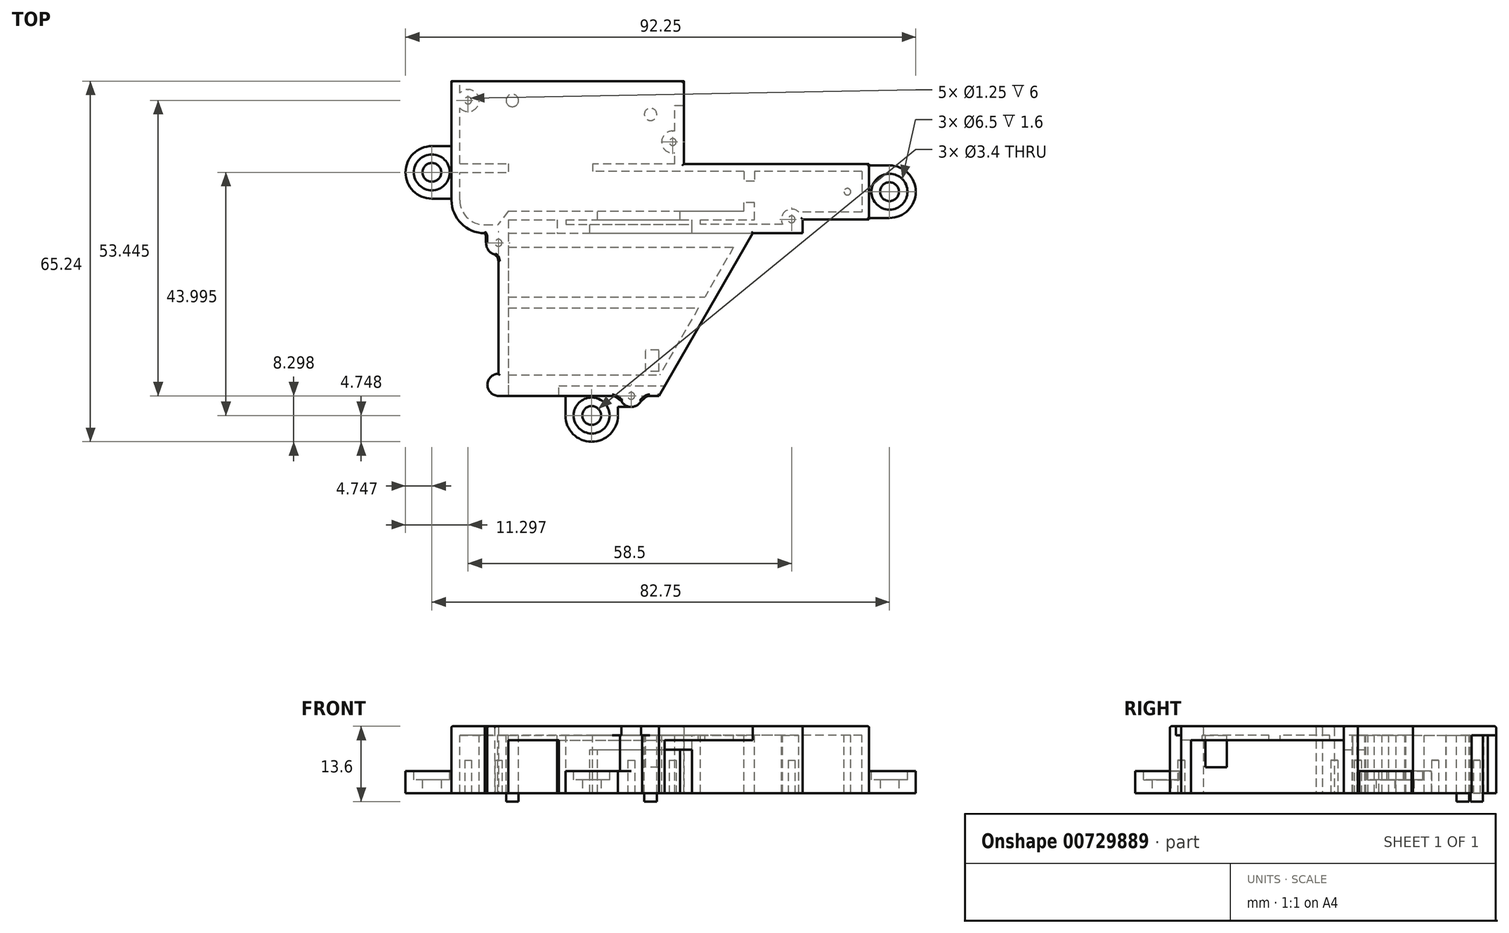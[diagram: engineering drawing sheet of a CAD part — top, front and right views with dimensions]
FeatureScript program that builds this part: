
annotation { "Feature Type Name" : "Feature", "Feature Type Description" : "" }
export const myFeature = defineFeature(function(context is Context, id is Id, definition is map)
    precondition{}
    {
        {
            var Q0;
            Q0=qCreatedBy(makeId("Top.planeOp"),FACE);
            var sketch = newSketch(context, id + "F0", { "sketchPlane" : qUnion([Q0])});
            skLineSegment(sketch, "E0.bottom", {"start": v(10.38, 28.25) * mm, "end": v(43.88, 28.25) * mm});
            skLineSegment(sketch, "E0.top", {"start": v(10.38, 18.25) * mm, "end": v(43.88, 18.25) * mm});
            skLineSegment(sketch, "E0.left", {"start": v(10.38, 28.25) * mm, "end": v(10.38, 18.25) * mm});
            skLineSegment(sketch, "E0.right", {"start": v(43.88, 28.25) * mm, "end": v(43.88, 18.25) * mm});
            skLineSegment(sketch, "E1.bottom", {"start": v(10.38, 18.25) * mm, "end": v(31.88, 18.25) * mm});
            skLineSegment(sketch, "E1.top", {"start": v(10.38, 15.75) * mm, "end": v(31.88, 15.75) * mm});
            skLineSegment(sketch, "E1.left", {"start": v(10.38, 18.25) * mm, "end": v(10.38, 15.75) * mm});
            skLineSegment(sketch, "E1.right", {"start": v(31.88, 18.25) * mm, "end": v(31.88, 15.75) * mm});
            skLineSegment(sketch, "E2.bottom", {"start": v(10.38, 28.25) * mm, "end": v(-31.62, 28.25) * mm});
            skLineSegment(sketch, "E2.top", {"start": v(10.38, 43.25) * mm, "end": v(-31.62, 43.25) * mm});
            skLineSegment(sketch, "E2.left", {"start": v(10.38, 28.25) * mm, "end": v(10.38, 43.25) * mm});
            skLineSegment(sketch, "E2.right", {"start": v(-31.62, 28.25) * mm, "end": v(-31.62, 43.25) * mm});
            skLineSegment(sketch, "E3.bottom", {"start": v(10.38, 15.75) * mm, "end": v(-25.62, 15.75) * mm});
            skLineSegment(sketch, "E3.left", {"start": v(10.38, 15.75) * mm, "end": v(10.38, 28.25) * mm});
            skLineSegment(sketch, "E3.right", {"start": v(-31.62, 21.75) * mm, "end": v(-31.62, 28.25) * mm});
            skLineSegment(sketch, "E4.bottom", {"start": v(-23.12, 15.75) * mm, "end": v(5.88, 15.75) * mm});
            skLineSegment(sketch, "E4.top", {"start": v(-23.12, -13.7) * mm, "end": v(5.88, -13.7) * mm});
            skLineSegment(sketch, "E4.left", {"start": v(-23.12, 15.75) * mm, "end": v(-23.12, -13.7) * mm});
            skLineSegment(sketch, "E4.right", {"start": v(5.88, 15.75) * mm, "end": v(5.88, -13.7) * mm});
            skCircle(sketch, "E5", {"center": v(-23.12, 14) * mm, "radius": 1.25 * mm, "construction": true});
            skArc(sketch, "E6", {"start": v(-23.12, 11.75) * mm, "mid": v(-25.24, 13.25) * mm, "end": v(-24.54, 15.75) * mm});
            skPoint(sketch, "E7.visualSharp", {"position": v(-31.62, 15.75) * mm});
            skArc(sketch, "E7.filletArc", {"start": v(-31.62, 21.75) * mm, "mid": v(-29.87, 17.51) * mm, "end": v(-25.62, 15.75) * mm});
            skFitSpline(sketch, "E8", {"points": [v(-25.62, 15.75) * mm, v(-25.37, 14) * mm], "startDerivative": vector(1.15, -1.43) * mm, "endDerivative": vector(0.25, -1.75) * mm});
            skFitSpline(sketch, "E9", {"points": [v(-23.79, 11.85) * mm, v(-23.12, 10.7) * mm], "startDerivative": vector(2, -1.63) * mm, "endDerivative": vector(0.58, -2) * mm});
            skCircle(sketch, "E10", {"center": v(-28.62, 39.75) * mm, "radius": 1 * mm, "construction": true});
            skCircle(sketch, "E11", {"center": v(-20.62, 39.75) * mm, "radius": 1.25 * mm, "construction": true});
            skCircle(sketch, "E12", {"center": v(-20.62, 39.75) * mm, "radius": 3.5 * mm, "construction": true});
            skCircle(sketch, "E13", {"center": v(4.38, 37.25) * mm, "radius": 1.25 * mm, "construction": true});
            skCircle(sketch, "E14", {"center": v(4.38, 37.25) * mm, "radius": 3.5 * mm, "construction": true});
            skCircle(sketch, "E15", {"center": v(8.38, 32.25) * mm, "radius": 1 * mm, "construction": true});
            skCircle(sketch, "E16", {"center": v(29.88, 18.25) * mm, "radius": 1 * mm, "construction": true});
            skArc(sketch, "E17", {"start": v(-23.12, -9.7) * mm, "mid": v(-25.12, -11.7) * mm, "end": v(-23.12, -13.7) * mm});
            skCircle(sketch, "E18", {"center": v(0.88, -13.7) * mm, "radius": 1 * mm, "construction": true});
            skArc(sketch, "E19", {"start": v(-1.12, -13.7) * mm, "mid": v(0.88, -15.7) * mm, "end": v(2.88, -13.7) * mm});
            skFitSpline(sketch, "E20", {"points": [v(-0.9, -14.6) * mm, v(-2.57, -13.7) * mm], "startDerivative": vector(-1.67, 0.9) * mm, "endDerivative": vector(-2.08, 0) * mm});
            skFitSpline(sketch, "E21", {"points": [v(2.65, -14.62) * mm, v(4.23, -13.7) * mm], "startDerivative": vector(1.58, 0.92) * mm, "endDerivative": vector(2.44, 0) * mm});
            skLineSegment(sketch, "E22", {"start": v(5.88, -13.7) * mm, "end": v(22.88, 15.75) * mm});
            skSolve(sketch);
        }
        {
            var Q0;
            {var subQ0=sQuery(id+"F0.wireOp",EDGE,"E9");var subQ3=sQuery(id+"F0.wireOp",EDGE,"E6");var subQ6=sQuery(id+"F0.wireOp",EDGE,"E17");var subQ7=sQuery(id+"F0.wireOp",EDGE,"E4.top");var subQ11=sQuery(id+"F0.wireOp",EDGE,"E21");var subQ13=sQuery(id+"F0.wireOp",EDGE,"E19");var subQ16=makeQuery(id+"F0.imprint","INTERSECT",VERTEX,{"disambiguationData":[OD(0.0)],"derivedFrom":[subQ7,subQ13]});var subQ17=sQuery(id+"F0.wireOp",EDGE,"E20");var subQ20=sQuery(id+"F0.wireOp",EDGE,"E3.bottom");var subQ23=sQuery(id+"F0.wireOp",EDGE,"E4.right");var subQ26=makeQuery(id+"F0.imprint","IMPRINT",EDGE,{"disambiguationData":[TD([[subQ16,-1.0]])],"derivedFrom":subQ7});var subQ28=makeQuery(id+"F0.imprint","IMPRINT",EDGE,{"derivedFrom":subQ23});var subQ29=makeQuery(id+"F0.imprint","IMPRINT",EDGE,{"derivedFrom":sQuery(id+"F0.wireOp",EDGE,"E2.bottom")});var subQ31=sQuery(id+"F0.wireOp",EDGE,"E1.left");var subQ32=makeQuery(id+"F0.imprint","IMPRINT",EDGE,{"derivedFrom":subQ31});var subQ33=sQuery(id+"F0.wireOp",EDGE,"E0.left");var subQ34=makeQuery(id+"F0.imprint","IMPRINT",EDGE,{"derivedFrom":subQ33});var subQ38=makeQuery(id+"F0.imprint","INTERSECT",VERTEX,{"derivedFrom":[subQ20,subQ3]});var subQ39=makeQuery(id+"F0.imprint","IMPRINT",EDGE,{"disambiguationData":[TD([[subQ38,1.0]])],"derivedFrom":subQ20});var subQ40=sQuery(id+"F0.wireOp",EDGE,"E8");Q0=qUnion([makeQuery(id+"F0.imprint","IMPRINT",FACE,{"disambiguationData":[TD([[subQ29,-1.0]])]}),makeQuery(id+"F0.imprint","IMPRINT",FACE,{"disambiguationData":[TD([[makeQuery(id+"F0.imprint","IMPRINT",EDGE,{"derivedFrom":subQ6}),1.0]])]}),makeQuery(id+"F0.imprint","IMPRINT",FACE,{"disambiguationData":[TD([[makeQuery(id+"F0.imprint","IMPRINT",EDGE,{"derivedFrom":sQuery(id+"F0.wireOp",EDGE,"E0.bottom")}),-1.0]])]}),makeQuery(id+"F0.imprint","IMPRINT",FACE,{"disambiguationData":[TD([[makeQuery(id+"F0.imprint","IMPRINT",EDGE,{"derivedFrom":subQ40}),1.0]])]}),makeQuery(id+"F0.imprint","IMPRINT",FACE,{"disambiguationData":[TD([[makeQuery(id+"F0.imprint","IMPRINT",EDGE,{"derivedFrom":subQ17}),-1.0]])]}),makeQuery(id+"F0.imprint","IMPRINT",FACE,{"disambiguationData":[TD([[makeQuery(id+"F0.imprint","IMPRINT",EDGE,{"derivedFrom":subQ11}),1.0]])]}),makeQuery(id+"F0.imprint","IMPRINT",FACE,{"disambiguationData":[TD([[makeQuery(id+"F0.imprint","IMPRINT",EDGE,{"derivedFrom":subQ0}),1.0]])]}),makeQuery(id+"F0.imprint","IMPRINT",FACE,{"disambiguationData":[TD([[subQ32,1.0]])]}),makeQuery(id+"F0.imprint","IMPRINT",FACE,{"disambiguationData":[TD([[subQ28,1.0]])]}),makeQuery(id+"F0.imprint","IMPRINT",FACE,{"disambiguationData":[TD([[subQ26,-1.0]])]}),makeQuery(id+"F0.imprint","IMPRINT",FACE,{"disambiguationData":[TD([[subQ39,1.0]])]}),makeQuery(id+"F0.imprint","IMPRINT",FACE,{"disambiguationData":[TD([[subQ34,-1.0]])]}),makeQuery(id+"F0.imprint","IMPRINT",FACE,{"disambiguationData":[TD([[subQ28,-1.0]])]})]);}
            extrude(context, id + "F1", {"entities" : qUnion([Q0]), "depth" : 1.6 * mm, "offsetDistance" : 25 * mm});
        }
        {
            var Q0;
            Q0=makeQuery(id+"F1.opExtrude","CAP_FACE",FACE,{"disambiguationData":[OSD([sQuery(id+"F0.wireOp",EDGE,"E0.bottom"),sQuery(id+"F0.wireOp",EDGE,"E0.top"),sQuery(id+"F0.wireOp",EDGE,"E0.right"),sQuery(id+"F0.wireOp",EDGE,"E1.top"),sQuery(id+"F0.wireOp",EDGE,"E1.right"),sQuery(id+"F0.wireOp",EDGE,"E2.top"),sQuery(id+"F0.wireOp",EDGE,"E2.left"),sQuery(id+"F0.wireOp",EDGE,"E2.right"),sQuery(id+"F0.wireOp",EDGE,"E3.right"),sQuery(id+"F0.wireOp",EDGE,"E4.top"),sQuery(id+"F0.wireOp",EDGE,"E4.left"),sQuery(id+"F0.wireOp",EDGE,"E6"),sQuery(id+"F0.wireOp",EDGE,"E7.filletArc"),sQuery(id+"F0.wireOp",EDGE,"E8"),sQuery(id+"F0.wireOp",EDGE,"E9"),sQuery(id+"F0.wireOp",EDGE,"E17"),sQuery(id+"F0.wireOp",EDGE,"E19"),sQuery(id+"F0.wireOp",EDGE,"E20"),sQuery(id+"F0.wireOp",EDGE,"E21"),sQuery(id+"F0.wireOp",EDGE,"E22")])],"isStart":true});
            var sketch = newSketch(context, id + "F2", { "sketchPlane" : qUnion([Q0])});
            skCircle(sketch, "E23", {"center": v(4.38, -37.25) * mm, "radius": 1.13 * mm});
            skCircle(sketch, "E24", {"center": v(-20.62, -39.75) * mm, "radius": 1.13 * mm});
            skSolve(sketch);
        }
        {
            var Q0;
            Q0 = qSketchRegion(id + "F2", true);
            extrude(context, id + "F3", {"entities" : qUnion([Q0]), "operationType" : NewBodyOperationType.ADD, "depth" : 12 * mm, "offsetDistance" : 25 * mm});
        }
        {
            var Q0;
            Q0=makeQuery(id+"F1.opExtrude","CAP_FACE",FACE,{"disambiguationData":[OSD([sQuery(id+"F0.wireOp",EDGE,"E0.bottom"),sQuery(id+"F0.wireOp",EDGE,"E0.top"),sQuery(id+"F0.wireOp",EDGE,"E0.right"),sQuery(id+"F0.wireOp",EDGE,"E1.top"),sQuery(id+"F0.wireOp",EDGE,"E1.right"),sQuery(id+"F0.wireOp",EDGE,"E2.top"),sQuery(id+"F0.wireOp",EDGE,"E2.left"),sQuery(id+"F0.wireOp",EDGE,"E2.right"),sQuery(id+"F0.wireOp",EDGE,"E3.right"),sQuery(id+"F0.wireOp",EDGE,"E4.top"),sQuery(id+"F0.wireOp",EDGE,"E4.left"),sQuery(id+"F0.wireOp",EDGE,"E6"),sQuery(id+"F0.wireOp",EDGE,"E7.filletArc"),sQuery(id+"F0.wireOp",EDGE,"E8"),sQuery(id+"F0.wireOp",EDGE,"E9"),sQuery(id+"F0.wireOp",EDGE,"E17"),sQuery(id+"F0.wireOp",EDGE,"E19"),sQuery(id+"F0.wireOp",EDGE,"E20"),sQuery(id+"F0.wireOp",EDGE,"E21"),sQuery(id+"F0.wireOp",EDGE,"E22")])],"isStart":false});
            var sketch = newSketch(context, id + "F4", { "sketchPlane" : qUnion([Q0])});
            skCircle(sketch, "E25", {"center": v(-28.62, 39.75) * mm, "radius": 0.62 * mm});
            skCircle(sketch, "E26", {"center": v(8.38, 32.25) * mm, "radius": 0.62 * mm});
            skCircle(sketch, "E27", {"center": v(29.88, 18.25) * mm, "radius": 0.62 * mm});
            skCircle(sketch, "E28", {"center": v(-23.12, 14) * mm, "radius": 0.62 * mm});
            skCircle(sketch, "E29", {"center": v(0.88, -13.7) * mm, "radius": 0.62 * mm});
            skSolve(sketch);
        }
        {
            var Q0;
            Q0=makeQuery(id+"F1.opExtrude","CAP_FACE",FACE,{"disambiguationData":[OSD([sQuery(id+"F0.wireOp",EDGE,"E0.bottom"),sQuery(id+"F0.wireOp",EDGE,"E0.top"),sQuery(id+"F0.wireOp",EDGE,"E0.right"),sQuery(id+"F0.wireOp",EDGE,"E1.top"),sQuery(id+"F0.wireOp",EDGE,"E1.right"),sQuery(id+"F0.wireOp",EDGE,"E2.top"),sQuery(id+"F0.wireOp",EDGE,"E2.left"),sQuery(id+"F0.wireOp",EDGE,"E2.right"),sQuery(id+"F0.wireOp",EDGE,"E3.right"),sQuery(id+"F0.wireOp",EDGE,"E4.top"),sQuery(id+"F0.wireOp",EDGE,"E4.left"),sQuery(id+"F0.wireOp",EDGE,"E6"),sQuery(id+"F0.wireOp",EDGE,"E7.filletArc"),sQuery(id+"F0.wireOp",EDGE,"E8"),sQuery(id+"F0.wireOp",EDGE,"E9"),sQuery(id+"F0.wireOp",EDGE,"E17"),sQuery(id+"F0.wireOp",EDGE,"E19"),sQuery(id+"F0.wireOp",EDGE,"E20"),sQuery(id+"F0.wireOp",EDGE,"E21"),sQuery(id+"F0.wireOp",EDGE,"E22")])],"isStart":true});
            var sketch = newSketch(context, id + "F5", { "sketchPlane" : qUnion([Q0])});
            skCircle(sketch, "E30", {"center": v(0.88, 13.7) * mm, "radius": 0.62 * mm});
            skCircle(sketch, "E31", {"center": v(-23.12, -14) * mm, "radius": 0.62 * mm});
            skCircle(sketch, "E32", {"center": v(29.88, -18.25) * mm, "radius": 0.62 * mm});
            skCircle(sketch, "E33", {"center": v(-28.62, -39.75) * mm, "radius": 0.62 * mm});
            skCircle(sketch, "E34", {"center": v(8.38, -32.25) * mm, "radius": 0.62 * mm});
            skSolve(sketch);
        }
        {
            var Q0;
            Q0=makeQuery(id+"F1.opExtrude","CAP_FACE",FACE,{"disambiguationData":[OSD([sQuery(id+"F0.wireOp",EDGE,"E0.bottom"),sQuery(id+"F0.wireOp",EDGE,"E0.top"),sQuery(id+"F0.wireOp",EDGE,"E0.right"),sQuery(id+"F0.wireOp",EDGE,"E1.top"),sQuery(id+"F0.wireOp",EDGE,"E1.right"),sQuery(id+"F0.wireOp",EDGE,"E2.top"),sQuery(id+"F0.wireOp",EDGE,"E2.left"),sQuery(id+"F0.wireOp",EDGE,"E2.right"),sQuery(id+"F0.wireOp",EDGE,"E3.right"),sQuery(id+"F0.wireOp",EDGE,"E4.top"),sQuery(id+"F0.wireOp",EDGE,"E4.left"),sQuery(id+"F0.wireOp",EDGE,"E6"),sQuery(id+"F0.wireOp",EDGE,"E7.filletArc"),sQuery(id+"F0.wireOp",EDGE,"E8"),sQuery(id+"F0.wireOp",EDGE,"E9"),sQuery(id+"F0.wireOp",EDGE,"E17"),sQuery(id+"F0.wireOp",EDGE,"E19"),sQuery(id+"F0.wireOp",EDGE,"E20"),sQuery(id+"F0.wireOp",EDGE,"E21"),sQuery(id+"F0.wireOp",EDGE,"E22")])],"isStart":true});
            var sketch = newSketch(context, id + "F6", { "sketchPlane" : qUnion([Q0])});
            skCircle(sketch, "E35", {"center": v(-28.62, -39.75) * mm, "radius": 2 * mm});
            skCircle(sketch, "E36", {"center": v(-23.12, -14) * mm, "radius": 1.85 * mm, "construction": true});
            skCircle(sketch, "E37", {"center": v(8.38, -32.25) * mm, "radius": 2 * mm});
            skCircle(sketch, "E38", {"center": v(29.88, -18.25) * mm, "radius": 1.85 * mm});
            skCircle(sketch, "E39", {"center": v(39.98, -23.25) * mm, "radius": 0.6 * mm});
            skLineSegment(sketch, "E40.0", {"start": v(-30.12, -21.75) * mm, "end": v(-30.12, -43.25) * mm});
            skArc(sketch, "E40.1", {"start": v(-30.12, -21.75) * mm, "mid": v(-28.8, -18.57) * mm, "end": v(-25.62, -17.25) * mm});
            skLineSegment(sketch, "E41.MirrorCS", {"start": v(-31.62, -27.26) * mm, "end": v(-31.62, -43.25) * mm});
            skLineSegment(sketch, "E42.MirrorCS", {"start": v(-31.62, -21.75) * mm, "end": v(-31.62, -27.26) * mm});
            skArc(sketch, "E43.MirrorCS", {"start": v(-31.62, -21.75) * mm, "mid": v(-29.87, -17.51) * mm, "end": v(-25.62, -15.75) * mm});
            skLineSegment(sketch, "E44.MirrorCS", {"start": v(-23.12, -15.75) * mm, "end": v(-23.12, 13.7) * mm});
            skLineSegment(sketch, "E45.MirrorCS", {"start": v(-23.12, -16.4) * mm, "end": v(-23.12, 13.7) * mm});
            skFitSpline(sketch, "E46.MirrorCS", {"points": [v(-23.79, -11.85) * mm, v(-23.12, -10.7) * mm], "startDerivative": vector(2, 1.63) * mm, "endDerivative": vector(0.58, 2) * mm});
            skArc(sketch, "E47.MirrorCS", {"start": v(-23.12, -11.75) * mm, "mid": v(-24.71, -12.41) * mm, "end": v(-25.37, -14) * mm});
            skFitSpline(sketch, "E48.MirrorCS", {"points": [v(-25.62, -15.75) * mm, v(-25.37, -14) * mm], "startDerivative": vector(1.15, 1.43) * mm, "endDerivative": vector(0.25, 1.75) * mm});
            skArc(sketch, "E49.MirrorCS", {"start": v(-23.12, 9.7) * mm, "mid": v(-25.12, 11.7) * mm, "end": v(-23.12, 13.7) * mm});
            skLineSegment(sketch, "E50.0", {"start": v(-21.32, -18.15) * mm, "end": v(-21.32, 13.7) * mm});
            skLineSegment(sketch, "E51", {"start": v(-23.12, 13.7) * mm, "end": v(-21.32, 13.7) * mm});
            skLineSegment(sketch, "E52", {"start": v(-25.62, -17.25) * mm, "end": v(-21.32, -17.25) * mm});
            skLineSegment(sketch, "E53.bottom", {"start": v(-21.32, -18.15) * mm, "end": v(-5.22, -18.15) * mm});
            skLineSegment(sketch, "E53.top", {"start": v(-21.32, -19.75) * mm, "end": v(-5.22, -19.75) * mm});
            skLineSegment(sketch, "E53.left", {"start": v(-21.32, -18.15) * mm, "end": v(-21.32, -19.75) * mm});
            skLineSegment(sketch, "E53.right", {"start": v(-5.22, -18.15) * mm, "end": v(-5.22, -19.75) * mm});
            skLineSegment(sketch, "E54.bottom", {"start": v(-12.52, -18.15) * mm, "end": v(-10.92, -18.15) * mm});
            skLineSegment(sketch, "E54.top", {"start": v(-12.52, -15.75) * mm, "end": v(-10.92, -15.75) * mm});
            skLineSegment(sketch, "E54.left", {"start": v(-12.52, -18.15) * mm, "end": v(-12.52, -15.75) * mm});
            skLineSegment(sketch, "E54.right", {"start": v(-10.92, -18.15) * mm, "end": v(-10.92, -15.75) * mm});
            skLineSegment(sketch, "E55.bottom", {"start": v(-10.92, -15.75) * mm, "end": v(-6.62, -15.75) * mm});
            skLineSegment(sketch, "E55.top", {"start": v(-10.92, -17.35) * mm, "end": v(-6.62, -17.35) * mm});
            skLineSegment(sketch, "E55.left", {"start": v(-10.92, -15.75) * mm, "end": v(-10.92, -17.35) * mm});
            skLineSegment(sketch, "E55.right", {"start": v(-6.62, -15.75) * mm, "end": v(-6.62, -17.35) * mm});
            skLineSegment(sketch, "E56", {"start": v(-21.32, -19.75) * mm, "end": v(-23.22, -17.25) * mm});
            skLineSegment(sketch, "E57.bottom", {"start": v(-30.12, -28.35) * mm, "end": v(-21.32, -28.35) * mm});
            skLineSegment(sketch, "E57.top", {"start": v(-30.12, -26.75) * mm, "end": v(-21.32, -26.75) * mm});
            skLineSegment(sketch, "E57.left", {"start": v(-30.12, -28.35) * mm, "end": v(-30.12, -26.75) * mm});
            skLineSegment(sketch, "E57.right", {"start": v(-21.32, -28.35) * mm, "end": v(-21.32, -26.75) * mm});
            skLineSegment(sketch, "E58.bottom", {"start": v(5.88, 13.7) * mm, "end": v(-12.22, 13.7) * mm});
            skLineSegment(sketch, "E58.top", {"start": v(5.88, 11.9) * mm, "end": v(-12.22, 11.9) * mm});
            skLineSegment(sketch, "E58.left", {"start": v(5.88, 13.7) * mm, "end": v(5.88, 11.9) * mm});
            skLineSegment(sketch, "E58.right", {"start": v(-12.22, 13.7) * mm, "end": v(-12.22, 11.9) * mm});
            skLineSegment(sketch, "E59", {"start": v(5.88, 11.9) * mm, "end": v(6.92, 11.9) * mm});
            skLineSegment(sketch, "E60", {"start": v(6.92, 11.9) * mm, "end": v(5.88, 13.7) * mm});
            skLineSegment(sketch, "E61.bottom", {"start": v(31.88, -15.75) * mm, "end": v(11.88, -15.75) * mm});
            skLineSegment(sketch, "E61.top", {"start": v(31.88, -17.35) * mm, "end": v(11.88, -17.35) * mm});
            skLineSegment(sketch, "E61.left", {"start": v(31.88, -15.75) * mm, "end": v(31.88, -17.35) * mm});
            skLineSegment(sketch, "E61.right", {"start": v(11.88, -15.75) * mm, "end": v(11.88, -17.35) * mm});
            skLineSegment(sketch, "E62.bottom", {"start": v(9.68, -18.15) * mm, "end": v(23.18, -18.15) * mm});
            skLineSegment(sketch, "E62.top", {"start": v(9.68, -19.75) * mm, "end": v(23.18, -19.75) * mm});
            skLineSegment(sketch, "E62.left", {"start": v(9.68, -18.15) * mm, "end": v(9.68, -19.75) * mm});
            skLineSegment(sketch, "E62.right", {"start": v(23.18, -18.15) * mm, "end": v(23.18, -19.75) * mm});
            skLineSegment(sketch, "E63.bottom", {"start": v(23.18, -19.75) * mm, "end": v(21.28, -19.75) * mm});
            skLineSegment(sketch, "E63.top", {"start": v(23.18, -21.25) * mm, "end": v(21.28, -21.25) * mm});
            skLineSegment(sketch, "E63.left", {"start": v(23.18, -19.75) * mm, "end": v(23.18, -21.25) * mm});
            skLineSegment(sketch, "E63.right", {"start": v(21.28, -19.75) * mm, "end": v(21.28, -21.25) * mm});
            skLineSegment(sketch, "E64.bottom", {"start": v(11.88, -17.35) * mm, "end": v(13.38, -17.35) * mm});
            skLineSegment(sketch, "E64.top", {"start": v(11.88, -18.15) * mm, "end": v(13.38, -18.15) * mm});
            skLineSegment(sketch, "E64.left", {"start": v(11.88, -17.35) * mm, "end": v(11.88, -18.15) * mm});
            skLineSegment(sketch, "E64.right", {"start": v(13.38, -17.35) * mm, "end": v(13.38, -18.15) * mm});
            skLineSegment(sketch, "E65.bottom", {"start": v(43.88, -18.25) * mm, "end": v(31.2, -18.25) * mm});
            skLineSegment(sketch, "E65.top", {"start": v(43.88, -19.55) * mm, "end": v(31.2, -19.55) * mm});
            skLineSegment(sketch, "E65.left", {"start": v(43.88, -18.25) * mm, "end": v(43.88, -19.55) * mm});
            skLineSegment(sketch, "E65.right", {"start": v(31.2, -18.25) * mm, "end": v(31.2, -19.55) * mm});
            skLineSegment(sketch, "E66.bottom", {"start": v(43.88, -28.25) * mm, "end": v(42.58, -28.25) * mm});
            skLineSegment(sketch, "E66.top", {"start": v(43.88, -19.55) * mm, "end": v(42.58, -19.55) * mm});
            skLineSegment(sketch, "E66.left", {"start": v(43.88, -28.25) * mm, "end": v(43.88, -19.55) * mm});
            skLineSegment(sketch, "E66.right", {"start": v(42.58, -28.25) * mm, "end": v(42.58, -19.55) * mm});
            skLineSegment(sketch, "E67.bottom", {"start": v(42.58, -28.25) * mm, "end": v(-6.12, -28.25) * mm});
            skLineSegment(sketch, "E67.top", {"start": v(42.58, -26.95) * mm, "end": v(-6.12, -26.95) * mm});
            skLineSegment(sketch, "E67.left", {"start": v(42.58, -28.25) * mm, "end": v(42.58, -26.95) * mm});
            skLineSegment(sketch, "E67.right", {"start": v(-6.12, -28.25) * mm, "end": v(-6.12, -26.95) * mm});
            skLineSegment(sketch, "E68.bottom", {"start": v(23.18, -26.95) * mm, "end": v(21.28, -26.95) * mm});
            skLineSegment(sketch, "E68.top", {"start": v(23.18, -25.15) * mm, "end": v(21.28, -25.15) * mm});
            skLineSegment(sketch, "E68.left", {"start": v(23.18, -26.95) * mm, "end": v(23.18, -25.15) * mm});
            skLineSegment(sketch, "E68.right", {"start": v(21.28, -26.95) * mm, "end": v(21.28, -25.15) * mm});
            skLineSegment(sketch, "E69.bottom", {"start": v(8.78, -28.25) * mm, "end": v(10.38, -28.25) * mm});
            skLineSegment(sketch, "E69.top", {"start": v(8.78, -38.85) * mm, "end": v(10.38, -38.85) * mm});
            skLineSegment(sketch, "E69.left", {"start": v(8.78, -28.25) * mm, "end": v(8.78, -38.85) * mm});
            skLineSegment(sketch, "E69.right", {"start": v(10.38, -28.25) * mm, "end": v(10.38, -38.85) * mm});
            skLineSegment(sketch, "E70", {"start": v(-5.22, -18.15) * mm, "end": v(9.68, -18.15) * mm, "construction": true});
            skLineSegment(sketch, "E71", {"start": v(9.68, -19.75) * mm, "end": v(-5.22, -19.75) * mm, "construction": true});
            skLineSegment(sketch, "E72", {"start": v(-6.62, -17.35) * mm, "end": v(11.88, -17.35) * mm, "construction": true});
            skLineSegment(sketch, "E73", {"start": v(-6.62, -15.75) * mm, "end": v(11.88, -15.75) * mm, "construction": true});
            skLineSegment(sketch, "E74", {"start": v(-31.62, -43.25) * mm, "end": v(-30.12, -43.25) * mm});
            skLineSegment(sketch, "E75", {"start": v(31.88, -17.35) * mm, "end": v(31.88, -18.25) * mm});
            skArc(sketch, "E76", {"start": v(-1.12, 13.7) * mm, "mid": v(0.88, 15.7) * mm, "end": v(2.88, 13.7) * mm});
            skSolve(sketch);
        }
        {
            var Q0;
            Q0 = qSketchRegion(id + "F6", true);
            var Q1;
            Q1 = qSketchRegion(id + "F5", true);
            extrude(context, id + "F7", {"entities" : qUnion([Q0, Q1]), "operationType" : NewBodyOperationType.ADD, "depth" : 10.5 * mm, "offsetDistance" : 25 * mm});
        }
        {
            var Q0;
            {var subQ7=sQuery(id+"F0.wireOp",EDGE,"E20");var subQ10=sQuery(id+"F0.wireOp",EDGE,"E17");var subQ11=sQuery(id+"F0.wireOp",EDGE,"E4.left");var subQ12=sQuery(id+"F0.wireOp",EDGE,"E4.top");var subQ15=sQuery(id+"F0.wireOp",EDGE,"E22");var subQ19=sQuery(id+"F0.wireOp",EDGE,"E1.top");var subQ26=sQuery(id+"F0.wireOp",EDGE,"E2.left");var subQ30=sQuery(id+"F0.wireOp",EDGE,"E2.top");Q0=makeQuery(id+"F7.boolean.opBoolean","SPLIT",FACE,{"disambiguationData":[TD([makeQuery(id+"F1.opExtrude","SWEPT_FACE",FACE,{"disambiguationData":[OSD([subQ19])]})])],"derivedFrom":makeQuery(id+"F1.opExtrude","CAP_FACE",FACE,{"disambiguationData":[OSD([sQuery(id+"F0.wireOp",EDGE,"E0.bottom"),sQuery(id+"F0.wireOp",EDGE,"E0.top"),sQuery(id+"F0.wireOp",EDGE,"E0.right"),subQ19,sQuery(id+"F0.wireOp",EDGE,"E1.right"),subQ30,subQ26,sQuery(id+"F0.wireOp",EDGE,"E2.right"),sQuery(id+"F0.wireOp",EDGE,"E3.right"),subQ12,subQ11,sQuery(id+"F0.wireOp",EDGE,"E6"),sQuery(id+"F0.wireOp",EDGE,"E7.filletArc"),sQuery(id+"F0.wireOp",EDGE,"E8"),sQuery(id+"F0.wireOp",EDGE,"E9"),subQ10,sQuery(id+"F0.wireOp",EDGE,"E19"),subQ7,sQuery(id+"F0.wireOp",EDGE,"E21"),subQ15])],"isStart":true})});}
            var sketch = newSketch(context, id + "F8", { "sketchPlane" : qUnion([Q0])});
            skLineSegment(sketch, "E77.bottom", {"start": v(-6.62, -15.75) * mm, "end": v(11.88, -15.75) * mm});
            skLineSegment(sketch, "E77.top", {"start": v(-6.62, -17.35) * mm, "end": v(11.88, -17.35) * mm});
            skLineSegment(sketch, "E77.left", {"start": v(-6.62, -15.75) * mm, "end": v(-6.62, -17.35) * mm});
            skLineSegment(sketch, "E77.right", {"start": v(11.88, -15.75) * mm, "end": v(11.88, -17.35) * mm});
            skLineSegment(sketch, "E78.bottom", {"start": v(-5.22, -18.15) * mm, "end": v(9.68, -18.15) * mm});
            skLineSegment(sketch, "E78.top", {"start": v(-5.22, -19.75) * mm, "end": v(9.68, -19.75) * mm});
            skLineSegment(sketch, "E78.left", {"start": v(-5.22, -18.15) * mm, "end": v(-5.22, -19.75) * mm});
            skLineSegment(sketch, "E78.right", {"start": v(9.68, -18.15) * mm, "end": v(9.68, -19.75) * mm});
            skSolve(sketch);
        }
        {
            var Q0;
            Q0 = qSketchRegion(id + "F8", true);
            extrude(context, id + "F9", {"entities" : qUnion([Q0]), "operationType" : NewBodyOperationType.ADD, "depth" : 2.6 * mm, "offsetDistance" : 25 * mm});
        }
        {
            var Q0;
            {var subQ1=sQuery(id+"F0.wireOp",EDGE,"E20");var subQ4=sQuery(id+"F0.wireOp",EDGE,"E17");var subQ5=sQuery(id+"F0.wireOp",EDGE,"E4.left");var subQ6=sQuery(id+"F0.wireOp",EDGE,"E4.top");var subQ14=sQuery(id+"F0.wireOp",EDGE,"E1.top");var subQ15=makeQuery(id+"F1.opExtrude","SWEPT_FACE",FACE,{"disambiguationData":[OSD([subQ14])]});var subQ22=sQuery(id+"F0.wireOp",EDGE,"E22");var subQ40=sQuery(id+"F0.wireOp",EDGE,"E2.left");var subQ44=sQuery(id+"F0.wireOp",EDGE,"E2.top");Q0=makeQuery(id+"F9.boolean.opBoolean","SPLIT",FACE,{"disambiguationData":[TD([subQ15])],"derivedFrom":makeQuery(id+"F7.boolean.opBoolean","SPLIT",FACE,{"disambiguationData":[TD([subQ15])],"derivedFrom":makeQuery(id+"F1.opExtrude","CAP_FACE",FACE,{"disambiguationData":[OSD([sQuery(id+"F0.wireOp",EDGE,"E0.bottom"),sQuery(id+"F0.wireOp",EDGE,"E0.top"),sQuery(id+"F0.wireOp",EDGE,"E0.right"),subQ14,sQuery(id+"F0.wireOp",EDGE,"E1.right"),subQ44,subQ40,sQuery(id+"F0.wireOp",EDGE,"E2.right"),sQuery(id+"F0.wireOp",EDGE,"E3.right"),subQ6,subQ5,sQuery(id+"F0.wireOp",EDGE,"E6"),sQuery(id+"F0.wireOp",EDGE,"E7.filletArc"),sQuery(id+"F0.wireOp",EDGE,"E8"),sQuery(id+"F0.wireOp",EDGE,"E9"),subQ4,sQuery(id+"F0.wireOp",EDGE,"E19"),subQ1,sQuery(id+"F0.wireOp",EDGE,"E21"),subQ22])],"isStart":true})})});}
            var sketch = newSketch(context, id + "F10", { "sketchPlane" : qUnion([Q0])});
            skLineSegment(sketch, "E79.bottom", {"start": v(-21.32, -15.75) * mm, "end": v(19.39, -15.75) * mm});
            skLineSegment(sketch, "E79.top", {"start": v(-21.32, -13.2) * mm, "end": v(19.39, -13.2) * mm});
            skLineSegment(sketch, "E79.left", {"start": v(-21.32, -15.75) * mm, "end": v(-21.32, -13.2) * mm});
            skLineSegment(sketch, "E79.right", {"start": v(19.39, -15.75) * mm, "end": v(19.39, -13.2) * mm});
            skLineSegment(sketch, "E80.bottom", {"start": v(-21.32, 13.7) * mm, "end": v(-12.22, 13.7) * mm});
            skLineSegment(sketch, "E80.top", {"start": v(-21.32, 9.9) * mm, "end": v(-12.22, 9.9) * mm});
            skLineSegment(sketch, "E80.left", {"start": v(-21.32, 13.7) * mm, "end": v(-21.32, 9.9) * mm});
            skLineSegment(sketch, "E80.right", {"start": v(-12.22, 13.7) * mm, "end": v(-12.22, 9.9) * mm});
            skLineSegment(sketch, "E81.bottom", {"start": v(-12.22, 9.9) * mm, "end": v(6.92, 9.9) * mm});
            skLineSegment(sketch, "E81.top", {"start": v(-12.22, 11.9) * mm, "end": v(6.92, 11.9) * mm});
            skLineSegment(sketch, "E81.left", {"start": v(-12.22, 9.9) * mm, "end": v(-12.22, 11.9) * mm});
            skLineSegment(sketch, "E81.right", {"start": v(6.92, 9.9) * mm, "end": v(6.92, 11.9) * mm});
            skLineSegment(sketch, "E82.bottom", {"start": v(-21.32, -4.2) * mm, "end": v(14.2, -4.2) * mm});
            skLineSegment(sketch, "E82.top", {"start": v(-21.32, -2.2) * mm, "end": v(14.2, -2.2) * mm});
            skLineSegment(sketch, "E82.left", {"start": v(-21.32, -2.2) * mm, "end": v(-21.32, -4.2) * mm});
            skLineSegment(sketch, "E82.right", {"start": v(14.2, -2.2) * mm, "end": v(14.2, -4.2) * mm, "construction": true});
            skLineSegment(sketch, "E83", {"start": v(6.92, 9.9) * mm, "end": v(8.07, 9.9) * mm, "construction": true});
            skLineSegment(sketch, "E84", {"start": v(14.2, -2.2) * mm, "end": v(15.06, -2.2) * mm, "construction": true});
            skLineSegment(sketch, "E85", {"start": v(19.39, -13.2) * mm, "end": v(13.04, -2.2) * mm});
            skLineSegment(sketch, "E86", {"start": v(14.2, -4.2) * mm, "end": v(6.05, 9.9) * mm});
            skLineSegment(sketch, "E87", {"start": v(6.92, 11.9) * mm, "end": v(22.88, -15.75) * mm});
            skLineSegment(sketch, "E88", {"start": v(22.88, -15.75) * mm, "end": v(19.39, -15.75) * mm});
            skLineSegment(sketch, "E89", {"start": v(13.04, -2.2) * mm, "end": v(14.2, -4.2) * mm, "construction": true});
            skSolve(sketch);
        }
        {
            var Q0;
            Q0 = qSketchRegion(id + "F10", true);
            extrude(context, id + "F11", {"entities" : qUnion([Q0]), "operationType" : NewBodyOperationType.ADD, "surfaceOperationType" : NewSurfaceOperationType.ADD, "depth" : .9 * mm, "offsetDistance" : 25 * mm});
        }
        {
            var Q0;
            {var subQ3=sQuery(id+"F0.wireOp",EDGE,"E20");var subQ6=sQuery(id+"F0.wireOp",EDGE,"E17");var subQ7=sQuery(id+"F0.wireOp",EDGE,"E4.left");var subQ8=sQuery(id+"F0.wireOp",EDGE,"E4.top");var subQ16=sQuery(id+"F0.wireOp",EDGE,"E1.top");var subQ17=makeQuery(id+"F1.opExtrude","SWEPT_FACE",FACE,{"disambiguationData":[OSD([subQ16])]});var subQ23=sQuery(id+"F0.wireOp",EDGE,"E22");var subQ40=sQuery(id+"F0.wireOp",EDGE,"E2.left");var subQ44=sQuery(id+"F0.wireOp",EDGE,"E2.top");Q0=makeQuery(id+"F11.boolean.opBoolean","SPLIT",FACE,{"disambiguationData":[TD([makeQuery(id+"F11.opExtrude","SWEPT_FACE",FACE,{"disambiguationData":[OSD([sQuery(id+"F10.wireOp",EDGE,"E82.top")])]})])],"derivedFrom":makeQuery(id+"F9.boolean.opBoolean","SPLIT",FACE,{"disambiguationData":[TD([subQ17])],"derivedFrom":makeQuery(id+"F7.boolean.opBoolean","SPLIT",FACE,{"disambiguationData":[TD([subQ17])],"derivedFrom":makeQuery(id+"F1.opExtrude","CAP_FACE",FACE,{"disambiguationData":[OSD([sQuery(id+"F0.wireOp",EDGE,"E0.bottom"),sQuery(id+"F0.wireOp",EDGE,"E0.top"),sQuery(id+"F0.wireOp",EDGE,"E0.right"),subQ16,sQuery(id+"F0.wireOp",EDGE,"E1.right"),subQ44,subQ40,sQuery(id+"F0.wireOp",EDGE,"E2.right"),sQuery(id+"F0.wireOp",EDGE,"E3.right"),subQ8,subQ7,sQuery(id+"F0.wireOp",EDGE,"E6"),sQuery(id+"F0.wireOp",EDGE,"E7.filletArc"),sQuery(id+"F0.wireOp",EDGE,"E8"),sQuery(id+"F0.wireOp",EDGE,"E9"),subQ6,sQuery(id+"F0.wireOp",EDGE,"E19"),subQ3,sQuery(id+"F0.wireOp",EDGE,"E21"),subQ23])],"isStart":true})})})});}
            var sketch = newSketch(context, id + "F12", { "sketchPlane" : qUnion([Q0])});
            skLineSegment(sketch, "E90.top", {"start": v(5.88, 5.4) * mm, "end": v(3.48, 5.4) * mm});
            skLineSegment(sketch, "E90.left", {"start": v(5.88, 9.3) * mm, "end": v(5.88, 5.4) * mm});
            skLineSegment(sketch, "E90.right", {"start": v(3.48, 9.3) * mm, "end": v(3.48, 5.4) * mm});
            skLineSegment(sketch, "E91", {"start": v(5.88, 9.3) * mm, "end": v(3.48, 9.3) * mm});
            skSolve(sketch);
        }
        {
            var Q0;
            Q0 = qSketchRegion(id + "F12", true);
            extrude(context, id + "F13", {"entities" : qUnion([Q0]), "operationType" : NewBodyOperationType.ADD, "depth" : 5.8 * mm, "offsetDistance" : 25 * mm});
        }
        {
            var Q0;
            Q0=makeQuery(id+"F7.boolean.opBoolean","MERGE",FACE,{"derivedFrom":[makeQuery(id+"F7.opExtrude","CAP_FACE",FACE,{"disambiguationData":[OSD([sQuery(id+"F5.wireOp",EDGE,"E31")])],"isStart":false}),makeQuery(id+"F7.opExtrude","CAP_FACE",FACE,{"disambiguationData":[OSD([sQuery(id+"F5.wireOp",EDGE,"E33")])],"isStart":false}),makeQuery(id+"F7.opExtrude","CAP_FACE",FACE,{"disambiguationData":[OSD([sQuery(id+"F6.wireOp",EDGE,"E35"),sQuery(id+"F6.wireOp",EDGE,"E40.0"),sQuery(id+"F6.wireOp",EDGE,"E40.1"),sQuery(id+"F6.wireOp",EDGE,"E41.MirrorCS"),sQuery(id+"F6.wireOp",EDGE,"E42.MirrorCS"),sQuery(id+"F6.wireOp",EDGE,"E43.MirrorCS"),sQuery(id+"F6.wireOp",EDGE,"E45.MirrorCS"),sQuery(id+"F6.wireOp",EDGE,"E46.MirrorCS"),sQuery(id+"F6.wireOp",EDGE,"E47.MirrorCS"),sQuery(id+"F6.wireOp",EDGE,"E48.MirrorCS"),sQuery(id+"F6.wireOp",EDGE,"E49.MirrorCS"),sQuery(id+"F6.wireOp",EDGE,"E50.0"),sQuery(id+"F6.wireOp",EDGE,"E51"),sQuery(id+"F6.wireOp",EDGE,"E52"),sQuery(id+"F6.wireOp",EDGE,"E53.bottom"),sQuery(id+"F6.wireOp",EDGE,"E53.top"),sQuery(id+"F6.wireOp",EDGE,"E53.right"),sQuery(id+"F6.wireOp",EDGE,"E54.top"),sQuery(id+"F6.wireOp",EDGE,"E54.left"),sQuery(id+"F6.wireOp",EDGE,"E54.right"),sQuery(id+"F6.wireOp",EDGE,"E55.bottom"),sQuery(id+"F6.wireOp",EDGE,"E55.top"),sQuery(id+"F6.wireOp",EDGE,"E55.right"),sQuery(id+"F6.wireOp",EDGE,"E56"),sQuery(id+"F6.wireOp",EDGE,"E57.bottom"),sQuery(id+"F6.wireOp",EDGE,"E57.top"),sQuery(id+"F6.wireOp",EDGE,"E57.right"),sQuery(id+"F6.wireOp",EDGE,"E74")])],"isStart":false})]});
            var sketch = newSketch(context, id + "F14", { "sketchPlane" : qUnion([Q0])});
            skCircle(sketch, "E92", {"center": v(-35.17, -26.75) * mm, "radius": 4.75 * mm});
            skLineSegment(sketch, "E93", {"start": v(-35.17, -22) * mm, "end": v(-31.62, -22) * mm});
            skLineSegment(sketch, "E94", {"start": v(-31.62, -22) * mm, "end": v(-31.62, -31.5) * mm});
            skLineSegment(sketch, "E95", {"start": v(-31.62, -31.5) * mm, "end": v(-35.17, -31.5) * mm});
            skCircle(sketch, "E96", {"center": v(-6.27, 17.24) * mm, "radius": 4.75 * mm});
            skLineSegment(sketch, "E97", {"start": v(-11.02, 17.24) * mm, "end": v(-11.02, 13.7) * mm});
            skLineSegment(sketch, "E98", {"start": v(-11.02, 13.7) * mm, "end": v(-1.52, 13.7) * mm});
            skLineSegment(sketch, "E99", {"start": v(-1.52, 13.7) * mm, "end": v(-1.52, 17.24) * mm});
            skLineSegment(sketch, "E100", {"start": v(-1.52, 15.7) * mm, "end": v(0.87, 15.7) * mm});
            skLineSegment(sketch, "E101", {"start": v(0.87, 15.7) * mm, "end": v(0.87, 13.7) * mm});
            skLineSegment(sketch, "E102", {"start": v(0.87, 13.7) * mm, "end": v(-1.52, 13.7) * mm});
            skCircle(sketch, "E103", {"center": v(47.58, -23.25) * mm, "radius": 4.75 * mm});
            skLineSegment(sketch, "E104.bottom", {"start": v(47.58, -18.5) * mm, "end": v(43.88, -18.5) * mm});
            skLineSegment(sketch, "E104.top", {"start": v(47.58, -28) * mm, "end": v(43.88, -28) * mm});
            skLineSegment(sketch, "E104.left", {"start": v(47.58, -18.5) * mm, "end": v(47.58, -28) * mm});
            skLineSegment(sketch, "E104.right", {"start": v(43.88, -18.5) * mm, "end": v(43.88, -28) * mm});
            skSolve(sketch);
        }
        {
            var Q0;
            Q0 = qSketchRegion(id + "F14", true);
            extrude(context, id + "F15", {"entities" : qUnion([Q0]), "operationType" : NewBodyOperationType.ADD, "oppositeDirection" : true, "depth" : 4 * mm, "offsetDistance" : 25 * mm});
        }
        {
            var Q0;
            Q0=makeQuery(id+"F15.opExtrude","CAP_FACE",FACE,{"disambiguationData":[OSD([sQuery(id+"F14.wireOp",EDGE,"E103"),sQuery(id+"F14.wireOp",EDGE,"E104.bottom"),sQuery(id+"F14.wireOp",EDGE,"E104.top"),sQuery(id+"F14.wireOp",EDGE,"E104.right")])],"isStart":false});
            var sketch = newSketch(context, id + "F16", { "sketchPlane" : qUnion([Q0])});
            skCircle(sketch, "E105", {"center": v(-35.17, 26.75) * mm, "radius": 3.25 * mm});
            skCircle(sketch, "E106", {"center": v(-6.27, -17.24) * mm, "radius": 3.25 * mm});
            skCircle(sketch, "E107", {"center": v(47.58, 23.25) * mm, "radius": 3.25 * mm});
            skSolve(sketch);
        }
        {
            var Q0;
            Q0 = qSketchRegion(id + "F16", true);
            extrude(context, id + "F17", {"entities" : qUnion([Q0]), "operationType" : NewBodyOperationType.REMOVE, "oppositeDirection" : true, "depth" : 1.6 * mm, "offsetDistance" : 25 * mm});
        }
        {
            var Q0;
            {var subQ14=sQuery(id+"F6.wireOp",EDGE,"E35");Q0=makeQuery(id+"F14.imprint","IMPRINT",FACE,{"disambiguationData":[TD([[makeQuery(id+"F14.imprint","IMPRINT",EDGE,{"derivedFrom":makeQuery(id+"F7.opExtrude","CAP_EDGE",EDGE,{"disambiguationData":[OSD([subQ14])],"isStart":false})}),1.0]])]});}
            var sketch = newSketch(context, id + "F18", { "sketchPlane" : qUnion([Q0])});
            skCircle(sketch, "E108", {"center": v(0.88, 13.7) * mm, "radius": 0.62 * mm});
            skCircle(sketch, "E109", {"center": v(-23.12, -14) * mm, "radius": 0.62 * mm});
            skCircle(sketch, "E110", {"center": v(29.88, -18.25) * mm, "radius": 0.62 * mm});
            skCircle(sketch, "E111", {"center": v(-28.62, -39.75) * mm, "radius": 0.62 * mm});
            skCircle(sketch, "E112", {"center": v(8.38, -32.25) * mm, "radius": 0.62 * mm});
            skCircle(sketch, "E113", {"center": v(-35.17, -26.75) * mm, "radius": 1.7 * mm});
            skCircle(sketch, "E114", {"center": v(-6.27, 17.24) * mm, "radius": 1.7 * mm});
            skCircle(sketch, "E115", {"center": v(47.58, -23.25) * mm, "radius": 1.7 * mm});
            skSolve(sketch);
        }
        {
            var Q0;
            Q0 = qSketchRegion(id + "F18", true);
            extrude(context, id + "F19", {"entities" : qUnion([Q0]), "operationType" : NewBodyOperationType.REMOVE, "oppositeDirection" : true, "depth" : 6 * mm, "offsetDistance" : 25 * mm});
        }
        {
            var Q0;
            Q0=makeQuery(id+"F1.opExtrude","CAP_EDGE",EDGE,{"disambiguationData":[OSD([sQuery(id+"F0.wireOp",EDGE,"E0.bottom")])],"isStart":false});
            var Q1;
            Q1=makeQuery(id+"F1.opExtrude","CAP_EDGE",EDGE,{"disambiguationData":[OSD([sQuery(id+"F0.wireOp",EDGE,"E0.right")])],"isStart":false});
            var Q2;
            Q2=makeQuery(id+"F1.opExtrude","CAP_EDGE",EDGE,{"disambiguationData":[OSD([sQuery(id+"F0.wireOp",EDGE,"E0.top")])],"isStart":false});
            var Q3;
            Q3=makeQuery(id+"F1.opExtrude","CAP_EDGE",EDGE,{"disambiguationData":[OSD([sQuery(id+"F0.wireOp",EDGE,"E1.right")])],"isStart":false});
            var Q4;
            Q4=makeQuery(id+"F1.opExtrude","CAP_EDGE",EDGE,{"disambiguationData":[OSD([sQuery(id+"F0.wireOp",EDGE,"E1.top")])],"isStart":false});
            var Q5;
            {var subQ0=sQuery(id+"F0.wireOp",EDGE,"E4.top");Q5=makeQuery(id+"F1.opExtrude","CAP_EDGE",EDGE,{"disambiguationData":[OSD([subQ0]),TDD([makeQuery(id+"F0.imprint","IMPRINT",EDGE,{"disambiguationData":[TD([[makeQuery(id+"F0.imprint","INTERSECT",VERTEX,{"derivedFrom":[subQ0,sQuery(id+"F0.wireOp",EDGE,"E20")]}),1.0]])],"derivedFrom":subQ0})])],"isStart":false});}
            var Q6;
            Q6=makeQuery(id+"F1.opExtrude","CAP_EDGE",EDGE,{"disambiguationData":[OSD([sQuery(id+"F0.wireOp",EDGE,"E20")])],"isStart":false});
            var Q7;
            Q7=makeQuery(id+"F1.opExtrude","CAP_EDGE",EDGE,{"disambiguationData":[OSD([sQuery(id+"F0.wireOp",EDGE,"E19")])],"isStart":false});
            var Q8;
            Q8=makeQuery(id+"F1.opExtrude","CAP_EDGE",EDGE,{"disambiguationData":[OSD([sQuery(id+"F0.wireOp",EDGE,"E21")])],"isStart":false});
            var Q9;
            {var subQ0=sQuery(id+"F0.wireOp",EDGE,"E4.top");Q9=makeQuery(id+"F1.opExtrude","CAP_EDGE",EDGE,{"disambiguationData":[OSD([subQ0]),TDD([makeQuery(id+"F0.imprint","IMPRINT",EDGE,{"disambiguationData":[TD([[makeQuery(id+"F0.imprint","INTERSECT",VERTEX,{"derivedFrom":[subQ0,sQuery(id+"F0.wireOp",EDGE,"E21")]}),-1.0]])],"derivedFrom":subQ0})])],"isStart":false});}
            var Q10;
            Q10=makeQuery(id+"F1.opExtrude","CAP_EDGE",EDGE,{"disambiguationData":[OSD([sQuery(id+"F0.wireOp",EDGE,"E17")])],"isStart":false});
            var Q11;
            Q11=makeQuery(id+"F1.opExtrude","CAP_EDGE",EDGE,{"disambiguationData":[OSD([sQuery(id+"F0.wireOp",EDGE,"E4.left")])],"isStart":false});
            var Q12;
            Q12=makeQuery(id+"F1.opExtrude","CAP_EDGE",EDGE,{"disambiguationData":[OSD([sQuery(id+"F0.wireOp",EDGE,"E7.filletArc")])],"isStart":false});
            var Q13;
            Q13=makeQuery(id+"F1.opExtrude","CAP_EDGE",EDGE,{"disambiguationData":[OSD([sQuery(id+"F0.wireOp",EDGE,"E8")])],"isStart":false});
            var Q14;
            Q14=makeQuery(id+"F1.opExtrude","CAP_EDGE",EDGE,{"disambiguationData":[OSD([sQuery(id+"F0.wireOp",EDGE,"E6")])],"isStart":false});
            var Q15;
            Q15=makeQuery(id+"F1.opExtrude","CAP_EDGE",EDGE,{"disambiguationData":[OSD([sQuery(id+"F0.wireOp",EDGE,"E9")])],"isStart":false});
            var Q16;
            Q16=makeQuery(id+"F1.opExtrude","CAP_EDGE",EDGE,{"disambiguationData":[OSD([sQuery(id+"F0.wireOp",EDGE,"E2.right"),sQuery(id+"F0.wireOp",EDGE,"E3.right")])],"isStart":false});
            var Q17;
            Q17=makeQuery(id+"F1.opExtrude","CAP_EDGE",EDGE,{"disambiguationData":[OSD([sQuery(id+"F0.wireOp",EDGE,"E2.top")])],"isStart":false});
            var Q18;
            Q18=makeQuery(id+"F1.opExtrude","CAP_EDGE",EDGE,{"disambiguationData":[OSD([sQuery(id+"F0.wireOp",EDGE,"E2.left")])],"isStart":false});
            var Q19;
            Q19=makeQuery(id+"F1.opExtrude","CAP_EDGE",EDGE,{"disambiguationData":[OSD([sQuery(id+"F0.wireOp",EDGE,"E22")])],"isStart":false});
            fillet(context, id + "F20", {"entities" : qUnion([Q0, Q1, Q2, Q3, Q4, Q5, Q6, Q7, Q8, Q9, Q10, Q11, Q12, Q13, Q14, Q15, Q16, Q17, Q18, Q19]), "radius" : .25 * mm, "tangentPropagation" : true, "allowEdgeOverflow" : false});
        }
    });
